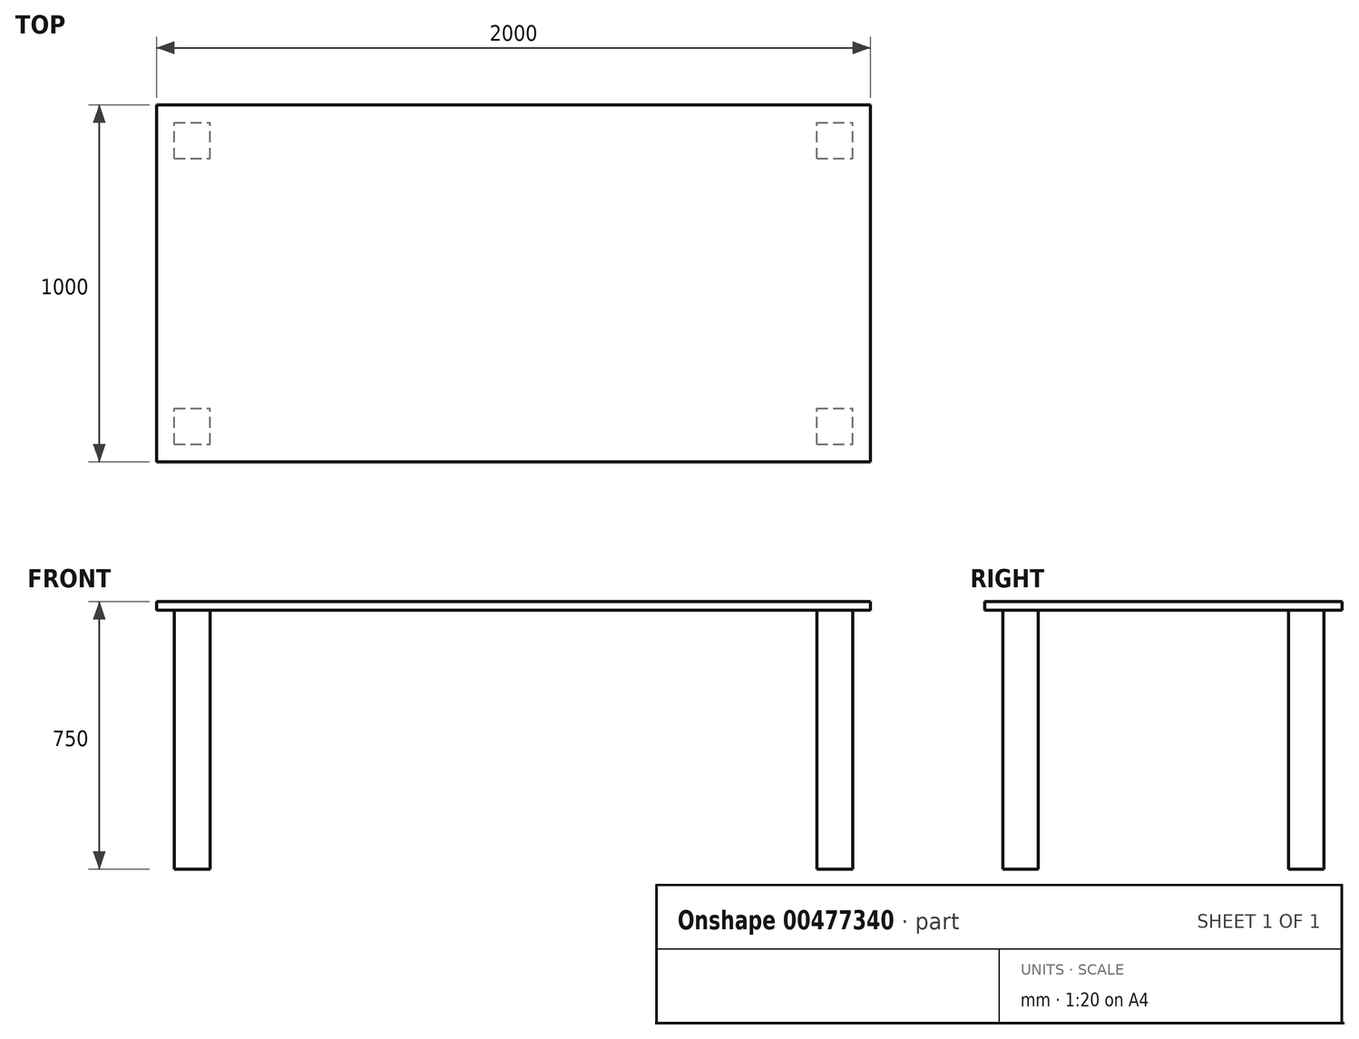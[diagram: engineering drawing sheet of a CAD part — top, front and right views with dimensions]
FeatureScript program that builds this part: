
annotation { "Feature Type Name" : "Feature", "Feature Type Description" : "" }
export const myFeature = defineFeature(function(context is Context, id is Id, definition is map)
    precondition{}
    {
        {
            var Q0;
            Q0=qCreatedBy(makeId("Top.planeOp"),FACE);
            var sketch = newSketch(context, id + "F0", { "sketchPlane" : qUnion([Q0])});
            skLineSegment(sketch, "E0.bottom", {"start": v(-280.31, 396.2) * mm, "end": v(1719.69, 396.2) * mm});
            skLineSegment(sketch, "E0.top", {"start": v(-280.31, -603.8) * mm, "end": v(1719.69, -603.8) * mm});
            skLineSegment(sketch, "E0.left", {"start": v(-280.31, 396.2) * mm, "end": v(-280.31, -603.8) * mm});
            skLineSegment(sketch, "E0.right", {"start": v(1719.69, 396.2) * mm, "end": v(1719.69, -603.8) * mm});
            skSolve(sketch);
        }
        {
            var Q0;
            Q0=makeQuery(id+"F0.imprint","IMPRINT",FACE,{"disambiguationData":[TD([[makeQuery(id+"F0.imprint","IMPRINT",EDGE,{"derivedFrom":sQuery(id+"F0.wireOp",EDGE,"E0.bottom")}),-1.0]])]});
            extrude(context, id + "F1", {"entities" : qUnion([Q0]), "depth" : 25 * mm});
        }
        {
            var Q0;
            Q0=makeQuery(id+"F1.opExtrude","CAP_FACE",FACE,{"disambiguationData":[OSD([sQuery(id+"F0.wireOp",EDGE,"E0.bottom"),sQuery(id+"F0.wireOp",EDGE,"E0.top"),sQuery(id+"F0.wireOp",EDGE,"E0.left"),sQuery(id+"F0.wireOp",EDGE,"E0.right")])],"isStart":true});
            var sketch = newSketch(context, id + "F2", { "sketchPlane" : qUnion([Q0])});
            skLineSegment(sketch, "E1.bottom", {"start": v(-230.31, 553.8) * mm, "end": v(-130.31, 553.8) * mm});
            skLineSegment(sketch, "E1.top", {"start": v(-230.31, 453.8) * mm, "end": v(-130.31, 453.8) * mm});
            skLineSegment(sketch, "E1.left", {"start": v(-230.31, 553.8) * mm, "end": v(-230.31, 453.8) * mm});
            skLineSegment(sketch, "E1.right", {"start": v(-130.31, 553.8) * mm, "end": v(-130.31, 453.8) * mm});
            skLineSegment(sketch, "E2.bottom", {"start": v(-230.31, -246.2) * mm, "end": v(-130.31, -246.2) * mm});
            skLineSegment(sketch, "E2.top", {"start": v(-230.31, -346.2) * mm, "end": v(-130.31, -346.2) * mm});
            skLineSegment(sketch, "E2.left", {"start": v(-230.31, -246.2) * mm, "end": v(-230.31, -346.2) * mm});
            skLineSegment(sketch, "E2.right", {"start": v(-130.31, -246.2) * mm, "end": v(-130.31, -346.2) * mm});
            skLineSegment(sketch, "E3.bottom", {"start": v(1569.69, 553.8) * mm, "end": v(1669.69, 553.8) * mm});
            skLineSegment(sketch, "E3.top", {"start": v(1569.69, 453.8) * mm, "end": v(1669.69, 453.8) * mm});
            skLineSegment(sketch, "E3.left", {"start": v(1569.69, 553.8) * mm, "end": v(1569.69, 453.8) * mm});
            skLineSegment(sketch, "E3.right", {"start": v(1669.69, 553.8) * mm, "end": v(1669.69, 453.8) * mm});
            skLineSegment(sketch, "E4.bottom", {"start": v(1569.69, -246.2) * mm, "end": v(1669.69, -246.2) * mm});
            skLineSegment(sketch, "E4.top", {"start": v(1569.69, -346.2) * mm, "end": v(1669.69, -346.2) * mm});
            skLineSegment(sketch, "E4.left", {"start": v(1569.69, -246.2) * mm, "end": v(1569.69, -346.2) * mm});
            skLineSegment(sketch, "E4.right", {"start": v(1669.69, -246.2) * mm, "end": v(1669.69, -346.2) * mm});
            skSolve(sketch);
        }
        {
            var Q0;
            Q0 = qSketchRegion(id + "F2", true);
            extrude(context, id + "F3", {"entities" : qUnion([Q0]), "operationType" : NewBodyOperationType.ADD, "depth" : 725 * mm, "offsetDistance" : 25 * mm});
        }
    });
